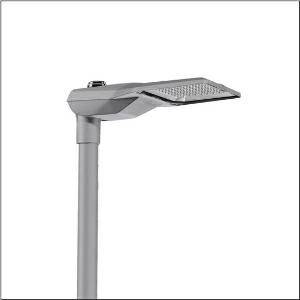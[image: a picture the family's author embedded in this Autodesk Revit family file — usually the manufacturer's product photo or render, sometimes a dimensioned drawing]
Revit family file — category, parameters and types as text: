
# Revit family: streetlight_sl_21_midi___pl52_5xe7h37n08mb_03fc
name_source: partatom
category: Lighting Fixtures
units: mm (PartAtom-declared; Revit-internal decimal feet)

## family parameters
Cut with Voids When Loaded = No
Host = Face
Light Source = No
Part Type = Normal
Room Calculation Point = No
Round Connector Dimension = Use Diameter
Shared = No

## types (1)
- --- (1 x LED, 17960 lm, 136 W, 3000K)
    Apparent Load = 136 VA
    CIE Flux Codes = 27 59 98 100 100
    Color Rendering = 70
    Color Temperature = 3000K
    Default Elevation = 1800 mm
    Description = Streetlight SL 21 midi, mast luminaire, primary light control with lens, of PMMA, primary optical cover: cover, of toughened safety glass, transparent, light distribution: PL52, light emission: direct distribution, primary light characteristic: asymmetric, installation type: side-entry, LED, 3G 2.5mm², High Power LED, rated luminous flux: 17.960lm, luminous efficacy: 132lm/W, light colour: 730, colour temperature: 3000K, control: overheat protection, pre-setting: linear dimming characteristic, constant luminous flux control, time-dependent luminous flux control, flexible luminous flux parameterisation, mains connection: 220..240V, AC, 50/60Hz, connection cable pre-assembled, cable length: 12,5m, wiring characteristics: H05VV-F, start of lifetime: 136W, end of service life: 142W, reduction: 61W, luminaire housing, of diecast aluminium (EN AC-44300), powder-coated, Siteco® metallic grey (DB 702S), corrosivity category C5 mid according to DIN EN ISO 12944, multi-level sealing system, sealing non-destructively replaceable, inclination adjustable: 0°, 5°, 10°, 15°, length: 644mm, width: 335mm, height: 110mm, spigot size: 42mm (side-entry), protection rating (complete): IP66, insulation class (complete): insulation class I (protective earthing), certification: CE, ENEC, ENEC+, VDE, impact resistance: IK09, permissible operating ambient temperature for outdoor applications: -40..+50°C, standard-compliant lighting for roads and squares, packaging unit: 1 piece

Light Distribution: PL52
    Height = 111 mm
    Lamp = 1 x LED
    Lamp Light Flux = 17960 lm
    Lamp Power = 136 W
    Lamp count = 1
    Length = 644 mm
    Luminous efficacy = 132 lm/W
    Manufacturer = Siteco
    ModVariant = No
    Model = 5XE7H37N08MB
    Number of Poles = 1
    OnlyDefault = Yes
    Power Factor = 1
    Product Name = Streetlight SL 21 midi | PL52
    Product group = mast luminaire | pylon top
    ProductGroupID = 6100
    Protection Class = Protection class I
    Protection Degree = IP 66
    RLX_Detail_Level = 1
    RLX_Emergency_Light_Flux = 0 lm
    RLX_Emergency_Type = 0
    RLX_Emergency_Type_DB = No
    RlxData = <blob elided: 99781 chars, md5=3f05796f>
    Socket = socket
    Standby Power = 0 W
    System Light Flux = 17960 lm
    System Power = 136 W
    Type Comments = factory setting: luminous flux: 100 % | dim-lin: 254 | 695 mA
    Type Image = l_1294377.jpg
    URL = http://relux.com
    VarID = @adj_106691
    Voltage = 0 V
    Weight = 0.00 kg
    Width = 336 mm

## geometry (parser evidence)
native form markers: Blend x4, Sweep x11
no freeform markers — native parametric forms only
